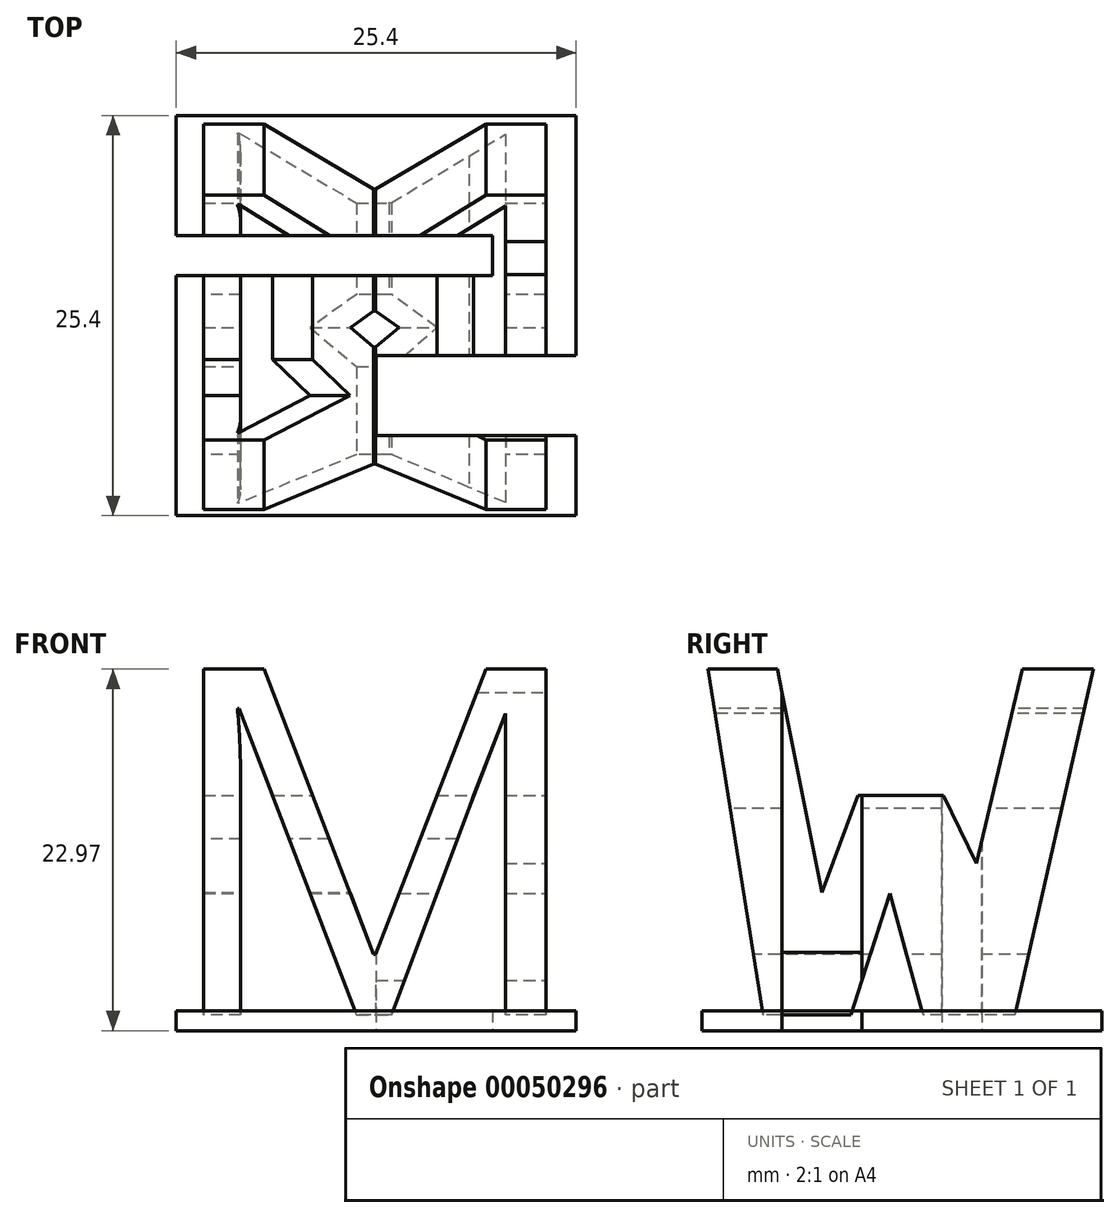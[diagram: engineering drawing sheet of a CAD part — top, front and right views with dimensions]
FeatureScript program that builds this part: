
annotation { "Feature Type Name" : "Feature", "Feature Type Description" : "" }
export const myFeature = defineFeature(function(context is Context, id is Id, definition is map)
    precondition{}
    {
        {
            var Q0;
            Q0=qCreatedBy(makeId("Right.planeOp"),FACE);
            var sketch = newSketch(context, id + "F0", { "sketchPlane" : qUnion([Q0])});
            skLineSegment(sketch, "E0", {"start": v(0, 0) * mm, "end": v(0, -25.4) * mm});
            skLineSegment(sketch, "E1", {"start": v(0, -25.4) * mm, "end": v(25.4, -25.4) * mm});
            skLineSegment(sketch, "E2", {"start": v(25.4, -25.4) * mm, "end": v(25.4, 0) * mm});
            skLineSegment(sketch, "E3", {"start": v(25.4, 0) * mm, "end": v(0, 0) * mm});
            skSolve(sketch);
        }
        {
            var Q0;
            Q0 = qSketchRegion(id + "F0", true);
            extrude(context, id + "F1", {"entities" : qUnion([Q0]), "depth" : 25.4 * mm});
        }
        {
            var Q0;
            Q0=qCreatedBy(makeId("Right.planeOp"),FACE);
            cPlane(context, id + "F2", {"entities" : qUnion([Q0]), "cplaneType" : CPlaneType.OFFSET, "offset" : 25.4 * mm, "width" : 152.4 * mm, "height" : 152.4 * mm});
        }
        {
            var Q0;
            Q0=qCreatedBy(id+"F2.planeOp",FACE);
            var sketch = newSketch(context, id + "F3", { "sketchPlane" : qUnion([Q0])});
            skLineSegment(sketch, "E4", {"start": v(0, 0) * mm, "end": v(24.31, 0) * mm});
            skLineSegment(sketch, "E5", {"start": v(0, 0) * mm, "end": v(4.05, -25.5) * mm});
            skLineSegment(sketch, "E6", {"start": v(4.05, -25.5) * mm, "end": v(9.1, -25.5) * mm});
            skLineSegment(sketch, "E7", {"start": v(9.1, -25.5) * mm, "end": v(11.93, -16.69) * mm});
            skLineSegment(sketch, "E8", {"start": v(11.93, -16.69) * mm, "end": v(14.33, -25.43) * mm});
            skLineSegment(sketch, "E9", {"start": v(14.33, -25.43) * mm, "end": v(19.62, -25.43) * mm});
            skLineSegment(sketch, "E10", {"start": v(19.62, -25.43) * mm, "end": v(25.41, 0) * mm});
            skLineSegment(sketch, "E11", {"start": v(25.41, 0) * mm, "end": v(20.92, 0) * mm});
            skLineSegment(sketch, "E12", {"start": v(20.92, 0) * mm, "end": v(17.4, -14.78) * mm});
            skLineSegment(sketch, "E13", {"start": v(17.4, -14.78) * mm, "end": v(15.32, -10.47) * mm});
            skLineSegment(sketch, "E14", {"start": v(15.32, -10.47) * mm, "end": v(9.9, -10.47) * mm});
            skLineSegment(sketch, "E15", {"start": v(9.9, -10.47) * mm, "end": v(7.62, -16.63) * mm});
            skLineSegment(sketch, "E16", {"start": v(7.62, -16.63) * mm, "end": v(4.3, 0) * mm});
            skLineSegment(sketch, "E17", {"start": v(4.3, 0) * mm, "end": v(0, 0) * mm});
            skLineSegment(sketch, "E18", {"start": v(0, 0) * mm, "end": v(25.41, 0) * mm});
            skLineSegment(sketch, "E19", {"start": v(25.41, 0) * mm, "end": v(25.41, -25.43) * mm});
            skLineSegment(sketch, "E20", {"start": v(25.41, -25.43) * mm, "end": v(0, -25.43) * mm});
            skLineSegment(sketch, "E21", {"start": v(0, -25.43) * mm, "end": v(0, 0) * mm});
            skLineSegment(sketch, "E22", {"start": v(25.41, 0) * mm, "end": v(0, 0) * mm});
            skSolve(sketch);
        }
        {
            var Q0;
            {var subQ1=sQuery(id+"F3.wireOp",EDGE,"E12");Q0=makeQuery(id+"F3.imprint","IMPRINT",FACE,{"disambiguationData":[TD([[makeQuery(id+"F3.imprint","IMPRINT",EDGE,{"derivedFrom":subQ1}),-1.0]])]});}
            var Q1;
            {var subQ0=sQuery(id+"F3.wireOp",EDGE,"E8");Q1=makeQuery(id+"F3.imprint","IMPRINT",FACE,{"disambiguationData":[TD([[makeQuery(id+"F3.imprint","IMPRINT",EDGE,{"derivedFrom":subQ0}),-1.0]])]});}
            var Q2;
            {var subQ0=sQuery(id+"F3.wireOp",EDGE,"E10");Q2=makeQuery(id+"F3.imprint","IMPRINT",FACE,{"disambiguationData":[TD([[makeQuery(id+"F3.imprint","IMPRINT",EDGE,{"derivedFrom":subQ0}),-1.0]])]});}
            var Q3;
            {var subQ0=sQuery(id+"F3.wireOp",EDGE,"E21");Q3=makeQuery(id+"F3.imprint","IMPRINT",FACE,{"disambiguationData":[TD([[makeQuery(id+"F3.imprint","IMPRINT",EDGE,{"derivedFrom":subQ0}),-1.0]])]});}
            extrude(context, id + "F4", {"entities" : qUnion([Q0, Q1, Q2, Q3]), "operationType" : NewBodyOperationType.REMOVE, "oppositeDirection" : true, "depth" : 38.1 * mm});
        }
        {
            var Q0;
            Q0=qCreatedBy(makeId("Front.planeOp"),FACE);
            var sketch = newSketch(context, id + "F5", { "sketchPlane" : qUnion([Q0])});
            skLineSegment(sketch, "E23", {"start": v(0, 0) * mm, "end": v(25.4, 0) * mm});
            skLineSegment(sketch, "E24", {"start": v(25.4, 0) * mm, "end": v(25.4, -25.4) * mm});
            skLineSegment(sketch, "E25", {"start": v(25.4, -25.4) * mm, "end": v(0, -25.4) * mm});
            skLineSegment(sketch, "E26", {"start": v(0, -25.4) * mm, "end": v(0, 0) * mm});
            skLineSegment(sketch, "E27", {"start": v(20.73, 0) * mm, "end": v(25.4, 0) * mm});
            skLineSegment(sketch, "E28", {"start": v(21.59, -25.4) * mm, "end": v(25.4, -25.4) * mm});
            skLineSegment(sketch, "E29", {"start": v(5.59, 0) * mm, "end": v(0, 0) * mm});
            skText(sketch, "E30", { "text": "M\n", "fontName": "OpenSans-Regular.ttf"});
            skPoint(sketch, "E30.firstSnap0", {"position": v(23.5, -25.4) * mm});
            skLineSegment(sketch, "E31", {"start": v(1.67, -2.23) * mm, "end": v(23.5, -2.23) * mm});
            skLineSegment(sketch, "E32", {"start": v(23.5, -24.39) * mm, "end": v(1.76, -24.39) * mm});
            skLineSegment(sketch, "E33", {"start": v(1.76, -24.39) * mm, "end": v(1.67, -2.23) * mm});
            skLineSegment(sketch, "E34", {"start": v(5.76, -2.23) * mm, "end": v(12.55, -20.2) * mm});
            skLineSegment(sketch, "E35", {"start": v(12.55, -20.2) * mm, "end": v(19.6, -2.23) * mm});
            skLineSegment(sketch, "E36", {"start": v(19.6, -2.23) * mm, "end": v(23.5, -2.23) * mm});
            skLineSegment(sketch, "E37", {"start": v(23.5, -24.39) * mm, "end": v(20.9, -24.39) * mm});
            skLineSegment(sketch, "E38", {"start": v(20.9, -24.39) * mm, "end": v(20.9, -5.06) * mm});
            skLineSegment(sketch, "E39", {"start": v(20.9, -5.06) * mm, "end": v(13.68, -24.39) * mm});
            skLineSegment(sketch, "E40", {"start": v(13.68, -24.39) * mm, "end": v(11.1, -24.39) * mm});
            skLineSegment(sketch, "E41", {"start": v(3.76, -4.89) * mm, "end": v(3.76, -24.39) * mm});
            skLineSegment(sketch, "E42", {"start": v(3.76, -24.39) * mm, "end": v(1.76, -24.39) * mm});
            const initialGuessF5  = {"E30": [-0.00128, -0.02439, 1, 0, 0.02215]};
            skSetInitialGuess(sketch, initialGuessF5);
            skSolve(sketch);
        }
        {
            var Q0;
            {var subQ2=sQuery(id+"F5.wireOp",EDGE,"E34");Q0=makeQuery(id+"F5.imprint","IMPRINT",FACE,{"disambiguationData":[TD([[makeQuery(id+"F5.imprint","IMPRINT",EDGE,{"derivedFrom":subQ2}),1.0]])]});}
            var Q1;
            {var subQ2=sQuery(id+"F5.wireOp",EDGE,"E30.sketch_text.stroke-0");Q1=makeQuery(id+"F5.imprint","IMPRINT",FACE,{"disambiguationData":[TD([[makeQuery(id+"F5.imprint","IMPRINT",EDGE,{"derivedFrom":subQ2}),1.0]])]});}
            var Q2;
            {var subQ0=sQuery(id+"F5.wireOp",EDGE,"E38");var subQ1=sQuery(id+"F5.wireOp",EDGE,"E30.sketch_text.stroke-16");var subQ2=makeQuery(id+"F5.imprint","INTERSECT",VERTEX,{"derivedFrom":[subQ1,subQ0]});Q2=makeQuery(id+"F5.imprint","IMPRINT",FACE,{"disambiguationData":[TD([[makeQuery(id+"F5.imprint","IMPRINT",EDGE,{"disambiguationData":[TD([[subQ2,-1.0]])],"derivedFrom":subQ1}),1.0]])]});}
            var Q3;
            Q3=makeQuery(id+"F5.imprint","IMPRINT",FACE,{"disambiguationData":[TD([[makeQuery(id+"F5.imprint","IMPRINT",EDGE,{"derivedFrom":sQuery(id+"F5.wireOp",EDGE,"E23")}),-1.0]])]});
            extrude(context, id + "F6", {"entities" : qUnion([Q0, Q1, Q2, Q3]), "operationType" : NewBodyOperationType.REMOVE, "oppositeDirection" : true, "depth" : 25.4 * mm});
        }
        {
            var Q0;
            Q0=qCreatedBy(makeId("Top.planeOp"),FACE);
            cPlane(context, id + "F7", {"entities" : qUnion([Q0]), "cplaneType" : CPlaneType.OFFSET, "offset" : 25.4 * mm, "oppositeDirection" : true, "width" : 152.4 * mm, "height" : 152.4 * mm});
        }
        {
            var Q0;
            Q0=qCreatedBy(id+"F7.planeOp",FACE);
            var sketch = newSketch(context, id + "F8", { "sketchPlane" : qUnion([Q0])});
            skLineSegment(sketch, "E43", {"start": v(0, 0) * mm, "end": v(25.4, 0) * mm});
            skLineSegment(sketch, "E44", {"start": v(25.4, 0) * mm, "end": v(25.4, 25.4) * mm});
            skLineSegment(sketch, "E45", {"start": v(25.4, 25.4) * mm, "end": v(0, 25.4) * mm});
            skLineSegment(sketch, "E46", {"start": v(0, 25.4) * mm, "end": v(0, 0) * mm});
            skLineSegment(sketch, "E47", {"start": v(25.4, 0) * mm, "end": v(25.4, 5.08) * mm});
            skLineSegment(sketch, "E48", {"start": v(25.4, 5.08) * mm, "end": v(12.7, 5.08) * mm});
            skLineSegment(sketch, "E49", {"start": v(12.7, 5.08) * mm, "end": v(12.7, 10.16) * mm});
            skLineSegment(sketch, "E50", {"start": v(12.7, 10.16) * mm, "end": v(25.4, 10.16) * mm});
            skLineSegment(sketch, "E51", {"start": v(25.4, 10.16) * mm, "end": v(25.4, 25.4) * mm});
            skLineSegment(sketch, "E52", {"start": v(0.9, 25.4) * mm, "end": v(0, 25.4) * mm});
            skLineSegment(sketch, "E53", {"start": v(0, 17.78) * mm, "end": v(20.1, 17.78) * mm});
            skLineSegment(sketch, "E54", {"start": v(20.1, 17.78) * mm, "end": v(20.1, 15.24) * mm});
            skLineSegment(sketch, "E55", {"start": v(20.1, 15.24) * mm, "end": v(0, 15.24) * mm});
            skLineSegment(sketch, "E56", {"start": v(0, 15.24) * mm, "end": v(0, 0) * mm});
            skSolve(sketch);
        }
        {
            var Q0;
            {var subQ0=sQuery(id+"F8.wireOp",EDGE,"E53");Q0=makeQuery(id+"F8.imprint","IMPRINT",FACE,{"disambiguationData":[TD([[makeQuery(id+"F8.imprint","IMPRINT",EDGE,{"derivedFrom":subQ0}),-1.0]])]});}
            var Q1;
            {var subQ0=sQuery(id+"F8.wireOp",EDGE,"E48");Q1=makeQuery(id+"F8.imprint","IMPRINT",FACE,{"disambiguationData":[TD([[makeQuery(id+"F8.imprint","IMPRINT",EDGE,{"derivedFrom":subQ0}),-1.0]])]});}
            extrude(context, id + "F9", {"entities" : qUnion([Q0, Q1]), "operationType" : NewBodyOperationType.REMOVE, "depth" : 25.4 * mm});
        }
        {
            var Q0;
            {var subQ1=sQuery(id+"F8.wireOp",EDGE,"E43");Q0=makeQuery(id+"F8.imprint","IMPRINT",FACE,{"disambiguationData":[TD([[makeQuery(id+"F8.imprint","IMPRINT",EDGE,{"derivedFrom":subQ1}),1.0]])]});}
            extrude(context, id + "F10", {"entities" : qUnion([Q0]), "depth" : 1.27 * mm});
        }
    });
